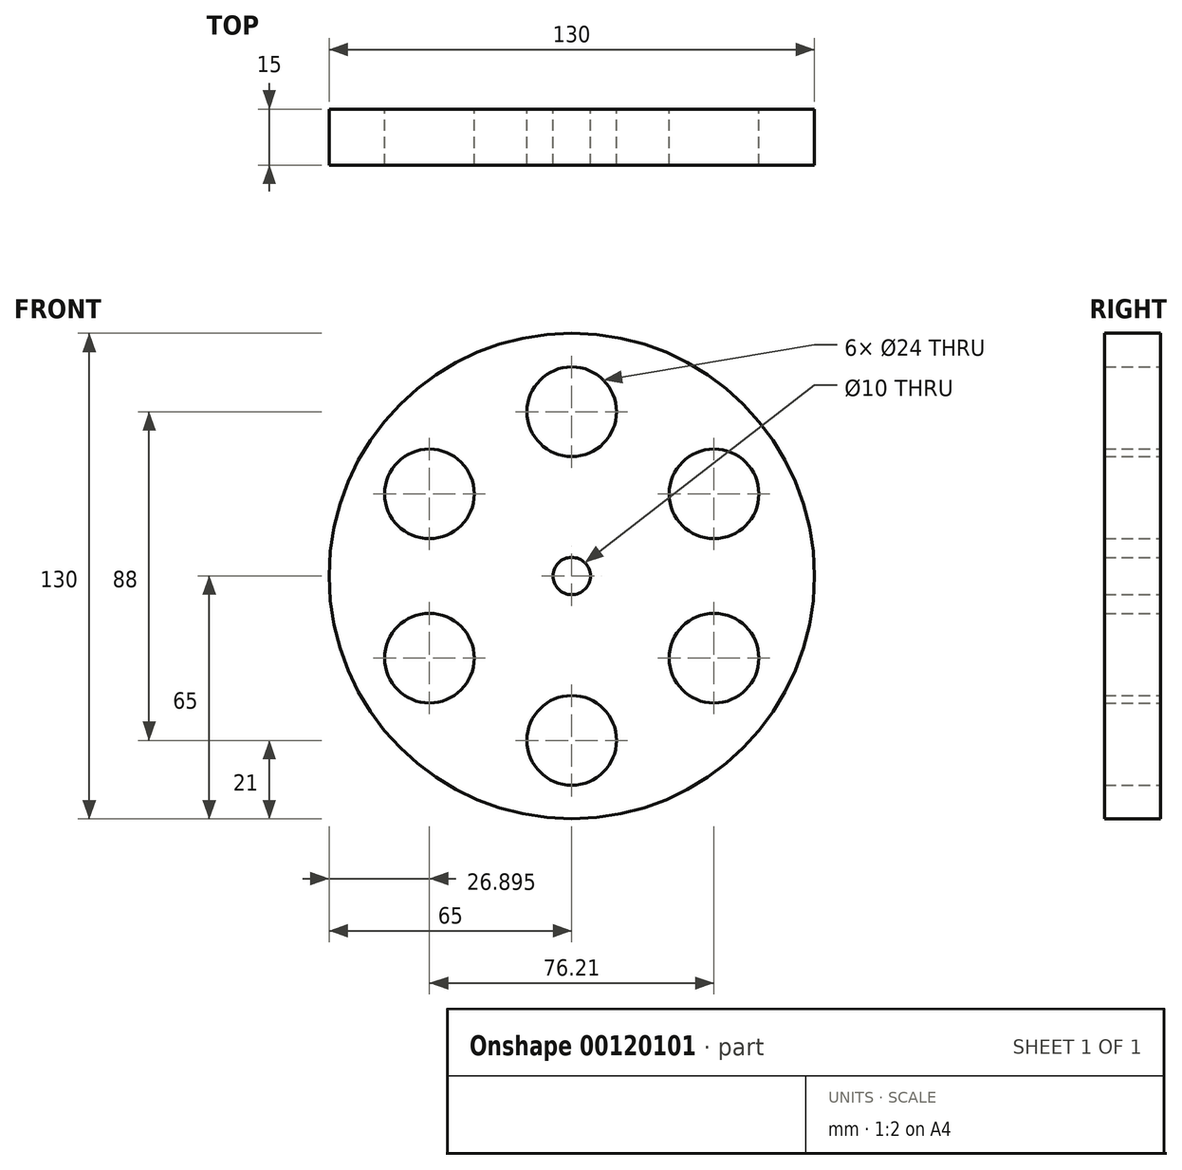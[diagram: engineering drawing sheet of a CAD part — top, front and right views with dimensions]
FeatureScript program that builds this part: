
annotation { "Feature Type Name" : "Feature", "Feature Type Description" : "" }
export const myFeature = defineFeature(function(context is Context, id is Id, definition is map)
    precondition{}
    {
        {
            var Q0;
            Q0=qCreatedBy(makeId("Front.planeOp"),FACE);
            var sketch = newSketch(context, id + "F0", { "sketchPlane" : qUnion([Q0])});
            skCircle(sketch, "E0", {"center": v(0, 0) * mm, "radius": 65 * mm});
            skCircle(sketch, "E1", {"center": v(0, 0) * mm, "radius": 5 * mm});
            skCircle(sketch, "E2.cCircle", {"center": v(0, 0) * mm, "radius": 44 * mm, "construction": true});
            skLineSegment(sketch, "E2.0", {"start": v(0, 44) * mm, "end": v(38.1, 22) * mm});
            skLineSegment(sketch, "E2.1", {"start": v(38.1, 22) * mm, "end": v(38.1, -22) * mm});
            skLineSegment(sketch, "E2.2", {"start": v(38.1, -22) * mm, "end": v(0, -44) * mm});
            skLineSegment(sketch, "E2.3", {"start": v(0, -44) * mm, "end": v(-38.1, -22) * mm});
            skLineSegment(sketch, "E2.4", {"start": v(-38.1, -22) * mm, "end": v(-38.1, 22) * mm});
            skLineSegment(sketch, "E2.5", {"start": v(-38.1, 22) * mm, "end": v(0, 44) * mm});
            skCircle(sketch, "E3", {"center": v(0, 44) * mm, "radius": 12 * mm});
            skCircle(sketch, "E4", {"center": v(38.1, 22) * mm, "radius": 12 * mm});
            skCircle(sketch, "E5", {"center": v(38.1, -22) * mm, "radius": 12 * mm});
            skCircle(sketch, "E6", {"center": v(0, -44) * mm, "radius": 12 * mm});
            skCircle(sketch, "E7", {"center": v(-38.1, -22) * mm, "radius": 12 * mm});
            skCircle(sketch, "E8", {"center": v(-38.1, 22) * mm, "radius": 12 * mm});
            skSolve(sketch);
        }
        {
            var Q0;
            Q0 = qSketchRegion(id + "F0", true);
            var Q1;
            Q1=makeQuery(id+"F0.imprint","IMPRINT",FACE,{"disambiguationData":[TD([[makeQuery(id+"F0.imprint","IMPRINT",EDGE,{"derivedFrom":sQuery(id+"F0.wireOp",EDGE,"E1")}),-1.0]])]});
            extrude(context, id + "F1", {"entities" : qUnion([Q0, Q1]), "endBound" : BoundingType.SYMMETRIC, "depth" : 15 * mm});
        }
    });
